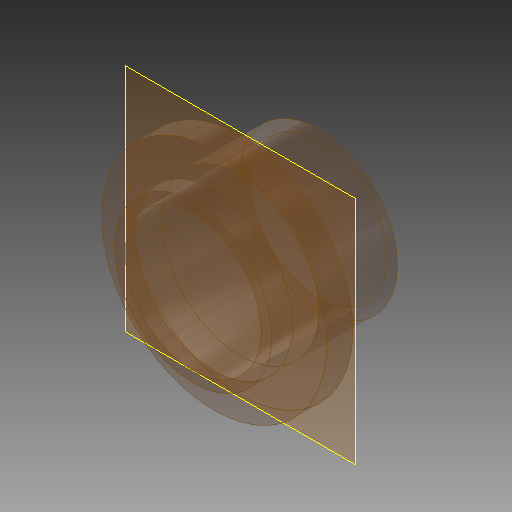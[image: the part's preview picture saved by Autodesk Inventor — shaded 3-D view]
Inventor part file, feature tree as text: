
AUTODESK INVENTOR PART (.ipt)
format: ipt  version: 2019 (Build 230136000, 136)  size: 138,752 bytes
history: native  units: mm
features: other x7, extrude x3, sketch x3
ambient origin geometry x8: Origin, YZ Plane, XZ Plane, XY Plane, X Axis, Y Axis, Z Axis, Center Point
bodies: Body1 (feature_tree)
feature tree (13):
  other  "Sólido1"
  other  "Plano de trabalho1"
  extrude  "Extrusão1"  Depth=15.0mm TaperAngle=0.0deg
  extrude  "Extrusão2"  Depth=5.0mm TaperAngle=0.0deg
  extrude  "Extrusão3"  [1 undecoded]
  sketch  "Esboço1"  dims[d0=2.0mm d1=15.0mm d2=0.0mm]
  other  "Referência1"
  sketch  "Esboço2"  dims[d3=43.0mm d4=5.0mm d5=0.0mm]
  other  "Referência2"
  sketch  "Esboço3"  dims[d6=4.0mm d7=0.0mm]
  other  "Referência3"
  other  "Conjunto Ambu.iam"
  other  "Corpo do Ambu:1"
note: 1 required parameter value undecoded (feature->parameter linkage not recoverable at this tier; creation-order binding heuristic only, values carry confidence <= 0.55)
